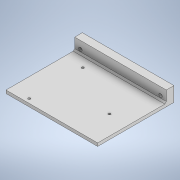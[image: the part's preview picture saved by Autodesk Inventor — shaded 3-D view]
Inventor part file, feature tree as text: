
AUTODESK INVENTOR PART (.ipt)
format: ipt  version: 2020.3 (Build 243373000, 373)  size: 283,648 bytes
history: native  units: mm
features: extrude x4, sketch x4, chamfer x2
ambient origin geometry x8: Origin, YZ Plane, XZ Plane, XY Plane, X Axis, Y Axis, Z Axis, Center Point
bodies: Solid1 (feature_tree)
feature tree (10):
  extrude  "Extrusion1"  Depth=120.0mm
  extrude  "Extrusion2"  Depth=5.0mm
  extrude  "Extrusion3"  Depth=15.0mm TaperAngle=0.0deg
  extrude  "Extrusion4"  Depth=10.0mm
  chamfer  "Chamfer2"  Distance=10.0mm
  chamfer  "Chamfer3"  Distance=70.0mm
  sketch  "Sketch1"  dims[d0=100.0mm d1=120.0mm]
  sketch  "Sketch2"  dims[d2=5.0mm d3=0.0mm d4=70.0mm]
  sketch  "Sketch3"  dims[d5=10.0mm d6=15.0mm d7=0.0mm]
  sketch  "Sketch4"  dims[d8=4.5mm d9=105.0mm d11=10.0mm d12=0.0mm d13=70.0mm d14=70.0mm d15=3.0mm d16=35.0mm d17=10.0mm d18=0.0mm d22=10.0mm d23=2.0mm d24=2.0mm d25=45.0deg d26=1.0mm d27=2.0mm d28=45.0deg]
